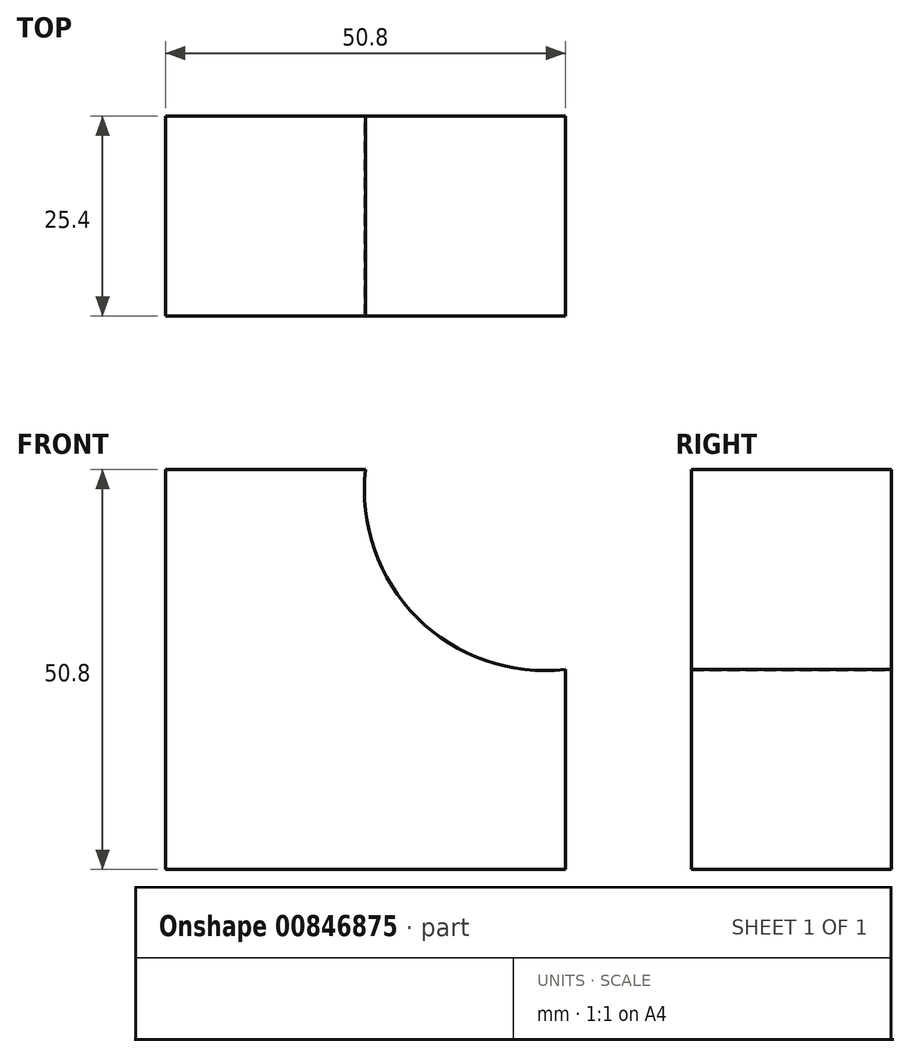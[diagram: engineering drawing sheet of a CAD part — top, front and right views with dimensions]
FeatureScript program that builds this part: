
annotation { "Feature Type Name" : "Feature", "Feature Type Description" : "" }
export const myFeature = defineFeature(function(context is Context, id is Id, definition is map)
    precondition{}
    {
        {
            var Q0;
            Q0=qCreatedBy(makeId("Front.planeOp"),FACE);
            var sketch = newSketch(context, id + "F0", { "sketchPlane" : qUnion([Q0])});
            skLineSegment(sketch, "E0", {"start": v(0, 0) * mm, "end": v(0, 50.8) * mm});
            skLineSegment(sketch, "E1", {"start": v(0, 0) * mm, "end": v(50.8, 0) * mm});
            skLineSegment(sketch, "E2", {"start": v(50.8, 0) * mm, "end": v(50.8, 25.4) * mm});
            skLineSegment(sketch, "E3", {"start": v(0, 50.8) * mm, "end": v(25.4, 50.8) * mm});
            skArc(sketch, "E4", {"start": v(25.4, 50.8) * mm, "mid": v(31.97, 31.97) * mm, "end": v(50.8, 25.4) * mm});
            skSolve(sketch);
        }
        {
            var Q0;
            Q0=qSketchRegion(id+"F0",true);
            extrude(context, id + "F1", {"entities" : qUnion([Q0]), "depth" : 25.4 * mm, "offsetDistance" : 25.4 * mm});
        }
    });
